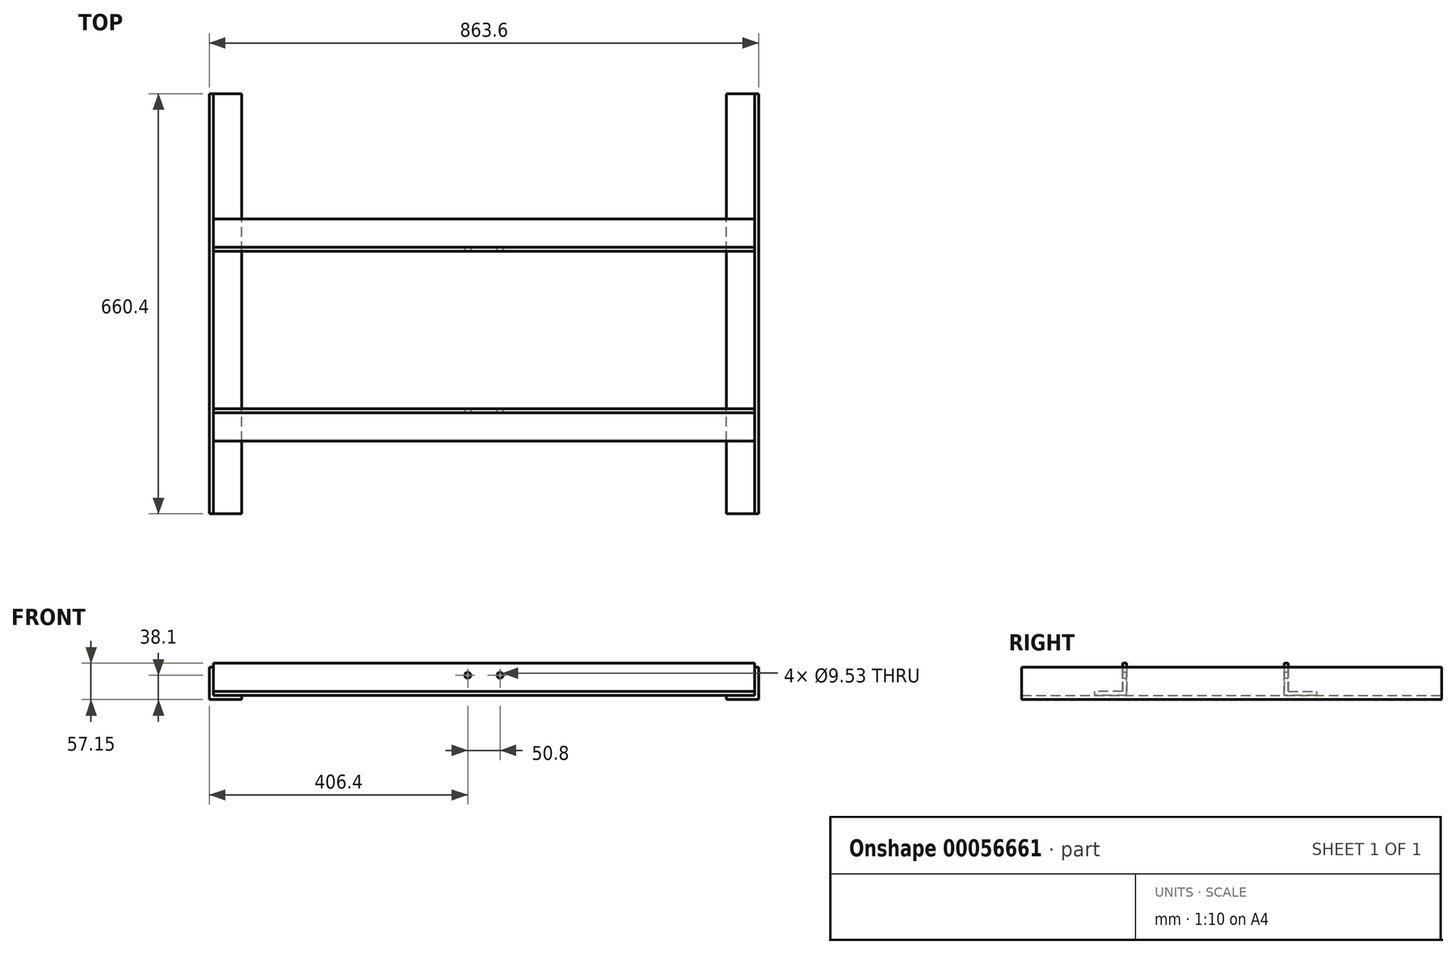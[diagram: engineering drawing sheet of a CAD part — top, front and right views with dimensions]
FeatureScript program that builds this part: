
annotation { "Feature Type Name" : "Feature", "Feature Type Description" : "" }
export const myFeature = defineFeature(function(context is Context, id is Id, definition is map)
    precondition{}
    {
        {
            var Q0;
            Q0=qCreatedBy(makeId("Front.planeOp"),FACE);
            var sketch = newSketch(context, id + "F0", { "sketchPlane" : qUnion([Q0])});
            skLineSegment(sketch, "E0", {"start": v(-431.8, 50.8) * mm, "end": v(-431.8, 0) * mm});
            skLineSegment(sketch, "E1", {"start": v(-431.8, 0) * mm, "end": v(-381, 0) * mm});
            skLineSegment(sketch, "E2", {"start": v(-381, 0) * mm, "end": v(-381, 6.35) * mm});
            skLineSegment(sketch, "E3", {"start": v(-381, 6.35) * mm, "end": v(-425.45, 6.35) * mm});
            skLineSegment(sketch, "E4", {"start": v(-425.45, 6.35) * mm, "end": v(-425.45, 50.8) * mm});
            skLineSegment(sketch, "E5", {"start": v(-425.45, 50.8) * mm, "end": v(-431.8, 50.8) * mm});
            skLineSegment(sketch, "E6.MirrorCS", {"start": v(381, 0) * mm, "end": v(381, 6.35) * mm});
            skLineSegment(sketch, "E7.MirrorCS", {"start": v(425.45, 50.8) * mm, "end": v(431.8, 50.8) * mm});
            skLineSegment(sketch, "E8.MirrorCS", {"start": v(381, 6.35) * mm, "end": v(425.45, 6.35) * mm});
            skLineSegment(sketch, "E9.MirrorCS", {"start": v(431.8, 50.8) * mm, "end": v(431.8, 0) * mm});
            skLineSegment(sketch, "E10.MirrorCS", {"start": v(425.45, 6.35) * mm, "end": v(425.45, 50.8) * mm});
            skLineSegment(sketch, "E11.MirrorCS", {"start": v(431.8, 0) * mm, "end": v(381, 0) * mm});
            skSolve(sketch);
        }
        {
            var Q0;
            Q0 = qSketchRegion(id + "F0", true);
            extrude(context, id + "F1", {"entities" : qUnion([Q0]), "endBound" : BoundingType.SYMMETRIC, "depth" : 660.4 * mm});
        }
        {
            var Q0;
            Q0=makeQuery(id+"F1.opExtrude","SWEPT_FACE",FACE,{"disambiguationData":[OSD([sQuery(id+"F0.wireOp",EDGE,"E4")])]});
            var sketch = newSketch(context, id + "F2", { "sketchPlane" : qUnion([Q0])});
            skLineSegment(sketch, "E12", {"start": v(-165.1, 6.35) * mm, "end": v(-215.9, 6.35) * mm});
            skLineSegment(sketch, "E13", {"start": v(-215.9, 6.35) * mm, "end": v(-215.9, 12.7) * mm});
            skLineSegment(sketch, "E14", {"start": v(-215.9, 12.7) * mm, "end": v(-171.45, 12.7) * mm});
            skLineSegment(sketch, "E15", {"start": v(-171.45, 12.7) * mm, "end": v(-171.45, 57.15) * mm});
            skLineSegment(sketch, "E16", {"start": v(-165.1, 6.35) * mm, "end": v(-165.1, 57.15) * mm});
            skLineSegment(sketch, "E17", {"start": v(-165.1, 57.15) * mm, "end": v(-171.45, 57.15) * mm});
            skLineSegment(sketch, "E18.MirrorCS", {"start": v(82.55, 57.15) * mm, "end": v(88.9, 57.15) * mm});
            skLineSegment(sketch, "E19.MirrorCS", {"start": v(133.35, 12.7) * mm, "end": v(88.9, 12.7) * mm});
            skLineSegment(sketch, "E20.MirrorCS", {"start": v(88.9, 12.7) * mm, "end": v(88.9, 57.15) * mm});
            skLineSegment(sketch, "E21.MirrorCS", {"start": v(82.55, 6.35) * mm, "end": v(82.55, 57.15) * mm});
            skLineSegment(sketch, "E22.MirrorCS", {"start": v(133.35, 6.35) * mm, "end": v(133.35, 12.7) * mm});
            skLineSegment(sketch, "E23.MirrorCS", {"start": v(82.55, 6.35) * mm, "end": v(133.35, 6.35) * mm});
            skSolve(sketch);
        }
        {
            var Q0;
            Q0 = qSketchRegion(id + "F2", true);
            var Q1;
            Q1=makeQuery(id+"F1.opExtrude","SWEPT_FACE",FACE,{"disambiguationData":[OSD([sQuery(id+"F0.wireOp",EDGE,"E10.MirrorCS")])]});
            extrude(context, id + "F3", {"entities" : qUnion([Q0]), "endBound" : BoundingType.UP_TO_SURFACE, "endBoundEntityFace" : qUnion([Q1]), "depth" : 25.4 * mm});
        }
        {
            var Q0;
            Q0=makeQuery(id+"F3.opExtrude","SWEPT_FACE",FACE,{"disambiguationData":[OSD([sQuery(id+"F2.wireOp",EDGE,"E15")])]});
            var sketch = newSketch(context, id + "F4", { "sketchPlane" : qUnion([Q0])});
            skCircle(sketch, "E24", {"center": v(-25.4, 38.1) * mm, "radius": 4.76 * mm});
            skCircle(sketch, "E25", {"center": v(25.4, 38.1) * mm, "radius": 4.76 * mm});
            skSolve(sketch);
        }
        {
            var Q0;
            Q0 = qSketchRegion(id + "F4", true);
            extrude(context, id + "F5", {"entities" : qUnion([Q0]), "operationType" : NewBodyOperationType.REMOVE, "endBound" : BoundingType.THROUGH_ALL, "oppositeDirection" : true, "depth" : 25.4 * mm});
        }
    });
